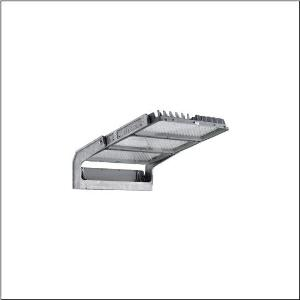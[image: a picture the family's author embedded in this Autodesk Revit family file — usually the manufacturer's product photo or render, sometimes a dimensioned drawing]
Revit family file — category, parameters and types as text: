
# Revit family: floodlight_fl_11_maxi_pro___rs08_5xa779229l01gb_31ec
name_source: partatom
category: Lighting Fixtures
units: mm (PartAtom-declared; Revit-internal decimal feet)

## family parameters
Cut with Voids When Loaded = No
Host = Face
Light Source = No
Part Type = Normal
Room Calculation Point = No
Round Connector Dimension = Use Diameter
Shared = No

## types (1)
- --- (1 x LED, 163120 lm, 1315 W, 5700K)
    Apparent Load = 1315 VA
    CIE Flux Codes = 70 87 98 100 100
    Color Rendering = 70
    Color Temperature = 5700K
    Default Elevation = 1800 mm
    Description = Floodlight FL 11  maxi  pro floodlight; light control with lens of PMMA; cover panel of toughened safety glass, transparent; light distribution: RS08, rotationally symmetric direct distribution, LED; colour temperature: 5700K, rated luminous flux: 163.120lm, colour rendering: CRI > 70, light colour: 757; luminous efficacy: 124lm/W; brightness control: DMX+RDM; with terminal, 6-pole, max. 2.5mm², mains connection: 220..240V/380..400V AC, 50/60Hz, surge voltage resistance: line to ground: 10kV, LED service life up to 100,000h L90. Typical operating time: 1000h per year., ECG replaceable separately, LED unit replaceable without ESD environment, dustproof LED module, dimming range 10..100%; 1315W floodlight with 3x LED unit of diecast aluminium, coated grey; length: 1.003mm / width: 651mm / height: 338mm; mounting bracket, of diecast aluminium, uncoated, natural, equipment: Power, protection rating (complete): IP66; insulation class (complete): insulation class I (protective earthing); certification: CE, ENEC, VDE; ball protection: ball impact resistant, only for outdoor installations in the designated locations, permissible operating ambient temperature: -45..+55°C, permissible storage temperature: -40..+85°Cpackaging unit: 1 piece

Light Distribution: RS08
    Height = 320 mm
    Lamp = 1 x LED
    Lamp Light Flux = 163120 lm
    Lamp Power = 1315 W
    Lamp count = 1
    Length = 1002 mm
    Luminous efficacy = 124 lm/W
    Manufacturer = Siteco
    ModVariant = No
    Model = 5XA779229L01GB
    Mounting Place = Ceiling
    Mounting Type = Surface mounted
    Number of Poles = 1
    OnlyDefault = Yes
    Power Factor = 1
    Product Name = Floodlight FL 11 maxi pro | RS08
    Product group = floodlight | ceiling mounted
    ProductGroupID = 303
    Protection Class = Protection class I
    Protection Degree = IP 66
    RLX_Detail_Level = 1
    RLX_Emergency_Light_Flux = 0 lm
    RLX_Emergency_Type = 0
    RLX_Emergency_Type_DB = No
    RlxData = <blob elided: 40253 chars, md5=4d2b548e>
    Socket = socket
    Standby Power = 0 W
    System Light Flux = 163120 lm
    System Power = 1315 W
    Type Comments = factory setting: luminous flux: 100 % | dim-lin: 255 | 895 mA
    Type Image = l_1356210.jpg
    URL = http://relux.com
    VarID = @adj_033677
    Voltage = 0 V
    Weight = 0.00 kg
    Width = 655 mm

## geometry (parser evidence)
native form markers: Blend x4, Sweep x12
no freeform markers — native parametric forms only
